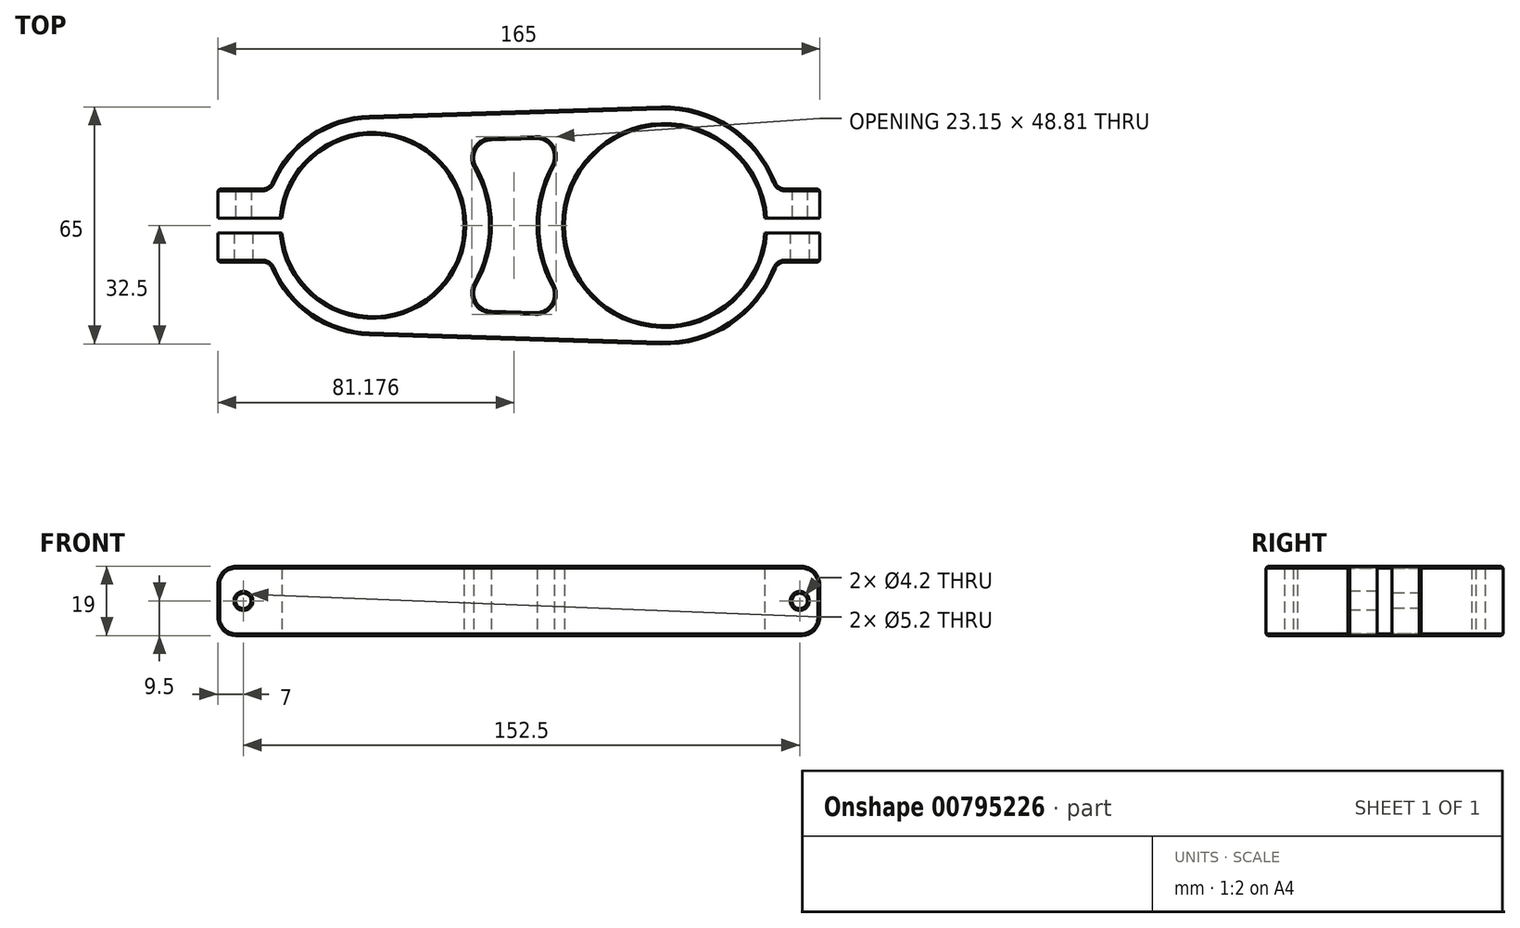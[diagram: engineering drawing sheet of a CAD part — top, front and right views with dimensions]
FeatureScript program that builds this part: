
annotation { "Feature Type Name" : "Feature", "Feature Type Description" : "" }
export const myFeature = defineFeature(function(context is Context, id is Id, definition is map)
    precondition{}
    {
        {
            var Q0;
            Q0=qCreatedBy(makeId("Top.planeOp"),FACE);
            var sketch = newSketch(context, id + "F0", { "sketchPlane" : qUnion([Q0])});
            skArc(sketch, "E0", {"start": v(-64.92, -2) * mm, "mid": v(-15, 0) * mm, "end": v(-64.92, 2) * mm});
            skArc(sketch, "E1", {"start": v(67.43, 2) * mm, "mid": v(12.5, 0) * mm, "end": v(67.43, -2) * mm});
            skArc(sketch, "E2", {"start": v(-40.94, 29.99) * mm, "mid": v(-57.7, 24.22) * mm, "end": v(-68.28, 10) * mm});
            skArc(sketch, "E3", {"start": v(38.98, -32.48) * mm, "mid": v(58.7, -26.58) * mm, "end": v(70.92, -10) * mm});
            skLineSegment(sketch, "E4", {"start": v(-40.94, 29.99) * mm, "end": v(38.98, 32.48) * mm});
            skLineSegment(sketch, "E5", {"start": v(38.98, -32.48) * mm, "end": v(-40.94, -29.99) * mm});
            skLineSegment(sketch, "E6.bottom", {"start": v(82.5, -10) * mm, "end": v(70.92, -10) * mm});
            skLineSegment(sketch, "E6.top", {"start": v(82.5, 10) * mm, "end": v(70.92, 10) * mm});
            skLineSegment(sketch, "E6.left", {"start": v(82.5, -10) * mm, "end": v(82.5, -2) * mm});
            skLineSegment(sketch, "E6.right", {"start": v(-82.5, -10) * mm, "end": v(-82.5, -2) * mm});
            skPoint(sketch, "E6.middle", {"position": v(0, 0) * mm});
            skLineSegment(sketch, "E7.bottom", {"start": v(82.5, -2) * mm, "end": v(67.43, -2) * mm});
            skLineSegment(sketch, "E7.top", {"start": v(82.5, 2) * mm, "end": v(67.43, 2) * mm});
            skLineSegment(sketch, "E8.trimOffspring", {"start": v(-68.28, 10) * mm, "end": v(-82.5, 10) * mm});
            skArc(sketch, "E9.trimOffspring", {"start": v(-68.28, -10) * mm, "mid": v(-57.7, -24.22) * mm, "end": v(-40.94, -29.99) * mm});
            skLineSegment(sketch, "E10.trimOffspring", {"start": v(-82.5, 2) * mm, "end": v(-82.5, 10) * mm});
            skPoint(sketch, "E7.right.end.orphan", {"position": v(-90, 2) * mm});
            skPoint(sketch, "E11.orphan", {"position": v(-90, -2) * mm});
            skLineSegment(sketch, "E12.trimOffspring", {"start": v(-68.28, -10) * mm, "end": v(-82.5, -10) * mm});
            skArc(sketch, "E13.trimOffspring", {"start": v(70.92, 10) * mm, "mid": v(58.7, 26.58) * mm, "end": v(38.98, 32.48) * mm});
            skLineSegment(sketch, "E14.trimOffspring", {"start": v(82.5, 2) * mm, "end": v(82.5, 10) * mm});
            skPoint(sketch, "E15.orphan", {"position": v(90, -2) * mm});
            skPoint(sketch, "E16.orphan", {"position": v(90, 2) * mm});
            skLineSegment(sketch, "E17.trimOffspring", {"start": v(-64.92, 2) * mm, "end": v(-82.5, 2) * mm});
            skLineSegment(sketch, "E18.trimOffspring", {"start": v(-64.92, -2) * mm, "end": v(-82.5, -2) * mm});
            skArc(sketch, "E19.0", {"start": v(-11.74, -16.06) * mm, "mid": v(-7.5, 0) * mm, "end": v(-11.74, 16.06) * mm});
            skLineSegment(sketch, "E19.1", {"start": v(4.6, -23.9) * mm, "end": v(-7.55, -23.53) * mm});
            skArc(sketch, "E19.2", {"start": v(9.16, 16.54) * mm, "mid": v(5, 0) * mm, "end": v(9.16, -16.54) * mm});
            skLineSegment(sketch, "E19.3", {"start": v(-7.55, 23.53) * mm, "end": v(4.6, 23.9) * mm});
            skPoint(sketch, "E20.visualSharp", {"position": v(-17.26, 23.22) * mm});
            skArc(sketch, "E20.filletArc", {"start": v(-7.55, 23.53) * mm, "mid": v(-11.76, 20.97) * mm, "end": v(-11.74, 16.06) * mm});
            skPoint(sketch, "E21.visualSharp", {"position": v(14.74, 24.22) * mm});
            skArc(sketch, "E21.filletArc", {"start": v(9.16, 16.54) * mm, "mid": v(9, 21.54) * mm, "end": v(4.6, 23.9) * mm});
            skPoint(sketch, "E22.visualSharp", {"position": v(14.74, -24.22) * mm});
            skArc(sketch, "E22.filletArc", {"start": v(4.6, -23.9) * mm, "mid": v(9, -21.54) * mm, "end": v(9.16, -16.54) * mm});
            skPoint(sketch, "E23.visualSharp", {"position": v(-17.26, -23.22) * mm});
            skArc(sketch, "E23.filletArc", {"start": v(-11.74, -16.06) * mm, "mid": v(-11.76, -20.97) * mm, "end": v(-7.55, -23.53) * mm});
            skSolve(sketch);
        }
        {
            var Q0;
            Q0=makeQuery(id+"F0.imprint","IMPRINT",FACE,{"disambiguationData":[TD([[makeQuery(id+"F0.imprint","IMPRINT",EDGE,{"derivedFrom":sQuery(id+"F0.wireOp",EDGE,"E0")}),-1.0]])]});
            extrude(context, id + "F1", {"entities" : qUnion([Q0]), "depth" : 19 * mm, "offsetDistance" : 25 * mm});
        }
        {
            var Q0;
            Q0=makeQuery(id+"F1.opExtrude","SWEPT_FACE",FACE,{"disambiguationData":[OSD([sQuery(id+"F0.wireOp",EDGE,"E12.trimOffspring")])]});
            var sketch = newSketch(context, id + "F2", { "sketchPlane" : qUnion([Q0])});
            skLineSegment(sketch, "E24", {"start": v(-82.5, 9.5) * mm, "end": v(94.03, 9.5) * mm, "construction": true});
            skCircle(sketch, "E25", {"center": v(-75.5, 9.5) * mm, "radius": 2.1 * mm});
            skCircle(sketch, "E26", {"center": v(77, 9.5) * mm, "radius": 2.1 * mm});
            skSolve(sketch);
        }
        {
            var Q0;
            Q0 = qSketchRegion(id + "F2", true);
            extrude(context, id + "F3", {"entities" : qUnion([Q0]), "operationType" : NewBodyOperationType.REMOVE, "oppositeDirection" : true, "depth" : 25 * mm, "offsetDistance" : 25 * mm});
        }
        {
            var Q0;
            Q0=makeQuery(id+"F1.opExtrude","SWEPT_FACE",FACE,{"disambiguationData":[OSD([sQuery(id+"F0.wireOp",EDGE,"E12.trimOffspring")])]});
            var sketch = newSketch(context, id + "F4", { "sketchPlane" : qUnion([Q0])});
            skCircle(sketch, "E27", {"center": v(-75.5, 9.5) * mm, "radius": 2.6 * mm});
            skSolve(sketch);
        }
        {
            var Q0;
            Q0 = qSketchRegion(id + "F4", true);
            extrude(context, id + "F5", {"entities" : qUnion([Q0]), "operationType" : NewBodyOperationType.REMOVE, "oppositeDirection" : true, "depth" : 10 * mm, "offsetDistance" : 25 * mm});
        }
        {
            var Q0;
            Q0=makeQuery(id+"F1.opExtrude","SWEPT_FACE",FACE,{"disambiguationData":[OSD([sQuery(id+"F0.wireOp",EDGE,"E6.bottom")])]});
            var sketch = newSketch(context, id + "F6", { "sketchPlane" : qUnion([Q0])});
            skCircle(sketch, "E28", {"center": v(77, 9.5) * mm, "radius": 2.6 * mm});
            skSolve(sketch);
        }
        {
            var Q0;
            Q0 = qSketchRegion(id + "F6", true);
            extrude(context, id + "F7", {"entities" : qUnion([Q0]), "operationType" : NewBodyOperationType.REMOVE, "oppositeDirection" : true, "depth" : 10 * mm, "offsetDistance" : 25 * mm});
        }
        {
            var Q0;
            Q0=makeQuery(id+"F1.opExtrude","CAP_EDGE",EDGE,{"disambiguationData":[OSD([sQuery(id+"F0.wireOp",EDGE,"E14.trimOffspring")])],"isStart":false});
            var Q1;
            Q1=makeQuery(id+"F1.opExtrude","CAP_EDGE",EDGE,{"disambiguationData":[OSD([sQuery(id+"F0.wireOp",EDGE,"E6.left")])],"isStart":false});
            var Q2;
            Q2=makeQuery(id+"F1.opExtrude","CAP_EDGE",EDGE,{"disambiguationData":[OSD([sQuery(id+"F0.wireOp",EDGE,"E14.trimOffspring")])],"isStart":true});
            var Q3;
            Q3=makeQuery(id+"F1.opExtrude","CAP_EDGE",EDGE,{"disambiguationData":[OSD([sQuery(id+"F0.wireOp",EDGE,"E6.left")])],"isStart":true});
            var Q4;
            Q4=makeQuery(id+"F1.opExtrude","CAP_EDGE",EDGE,{"disambiguationData":[OSD([sQuery(id+"F0.wireOp",EDGE,"E6.right")])],"isStart":true});
            var Q5;
            Q5=makeQuery(id+"F1.opExtrude","CAP_EDGE",EDGE,{"disambiguationData":[OSD([sQuery(id+"F0.wireOp",EDGE,"E6.right")])],"isStart":false});
            var Q6;
            Q6=makeQuery(id+"F1.opExtrude","CAP_EDGE",EDGE,{"disambiguationData":[OSD([sQuery(id+"F0.wireOp",EDGE,"E10.trimOffspring")])],"isStart":false});
            var Q7;
            Q7=makeQuery(id+"F1.opExtrude","CAP_EDGE",EDGE,{"disambiguationData":[OSD([sQuery(id+"F0.wireOp",EDGE,"E10.trimOffspring")])],"isStart":true});
            fillet(context, id + "F8", {"entities" : qUnion([Q0, Q1, Q2, Q3, Q4, Q5, Q6, Q7]), "radius" : 5 * mm, "tangentPropagation" : true, "allowEdgeOverflow" : false});
        }
        {
            var Q0;
            Q0=makeQuery(id+"F1.opExtrude","CAP_EDGE",EDGE,{"disambiguationData":[OSD([sQuery(id+"F0.wireOp",EDGE,"E0")])],"isStart":true});
            var Q1;
            Q1=makeQuery(id+"F1.opExtrude","CAP_EDGE",EDGE,{"disambiguationData":[OSD([sQuery(id+"F0.wireOp",EDGE,"E1")])],"isStart":true});
            var Q2;
            Q2=makeQuery(id+"F1.opExtrude","CAP_EDGE",EDGE,{"disambiguationData":[OSD([sQuery(id+"F0.wireOp",EDGE,"E1")])],"isStart":false});
            var Q3;
            Q3=makeQuery(id+"F1.opExtrude","CAP_EDGE",EDGE,{"disambiguationData":[OSD([sQuery(id+"F0.wireOp",EDGE,"E0")])],"isStart":false});
            chamfer(context, id + "F9", {"entities" : qUnion([Q0, Q1, Q2, Q3]), "width" : .5 * mm, "tangentPropagation" : true});
        }
        {
            var Q0;
            Q0=makeQuery(id+"F1.opExtrude","CAP_EDGE",EDGE,{"disambiguationData":[OSD([sQuery(id+"F0.wireOp",EDGE,"E19.3")])],"isStart":false});
            var Q1;
            Q1=makeQuery(id+"F1.opExtrude","CAP_EDGE",EDGE,{"disambiguationData":[OSD([sQuery(id+"F0.wireOp",EDGE,"E19.2")])],"isStart":true});
            chamfer(context, id + "F10", {"entities" : qUnion([Q0, Q1]), "width" : .5 * mm, "tangentPropagation" : true});
        }
        {
            var Q0;
            Q0=makeQuery(id+"F1.opExtrude","SWEPT_EDGE",EDGE,{"disambiguationData":[OSD([sQuery(id+"F0.wireOp",EDGE,"E2"),sQuery(id+"F0.wireOp",EDGE,"E8.trimOffspring")])]});
            var Q1;
            Q1=makeQuery(id+"F1.opExtrude","SWEPT_EDGE",EDGE,{"disambiguationData":[OSD([sQuery(id+"F0.wireOp",EDGE,"E9.trimOffspring"),sQuery(id+"F0.wireOp",EDGE,"E12.trimOffspring")])]});
            var Q2;
            Q2=makeQuery(id+"F1.opExtrude","SWEPT_EDGE",EDGE,{"disambiguationData":[OSD([sQuery(id+"F0.wireOp",EDGE,"E3"),sQuery(id+"F0.wireOp",EDGE,"E6.bottom")])]});
            var Q3;
            Q3=makeQuery(id+"F1.opExtrude","SWEPT_EDGE",EDGE,{"disambiguationData":[OSD([sQuery(id+"F0.wireOp",EDGE,"E6.top"),sQuery(id+"F0.wireOp",EDGE,"E13.trimOffspring")])]});
            fillet(context, id + "F11", {"entities" : qUnion([Q0, Q1, Q2, Q3]), "radius" : 3 * mm, "tangentPropagation" : true, "allowEdgeOverflow" : false});
        }
        {
            var Q0;
            Q0=makeQuery(id+"F1.opExtrude","CAP_EDGE",EDGE,{"disambiguationData":[OSD([sQuery(id+"F0.wireOp",EDGE,"E13.trimOffspring")])],"isStart":false});
            var Q1;
            Q1=makeQuery(id+"F1.opExtrude","CAP_EDGE",EDGE,{"disambiguationData":[OSD([sQuery(id+"F0.wireOp",EDGE,"E3")])],"isStart":false});
            chamfer(context, id + "F12", {"entities" : qUnion([Q0, Q1]), "width" : .5 * mm, "tangentPropagation" : true});
        }
    });
